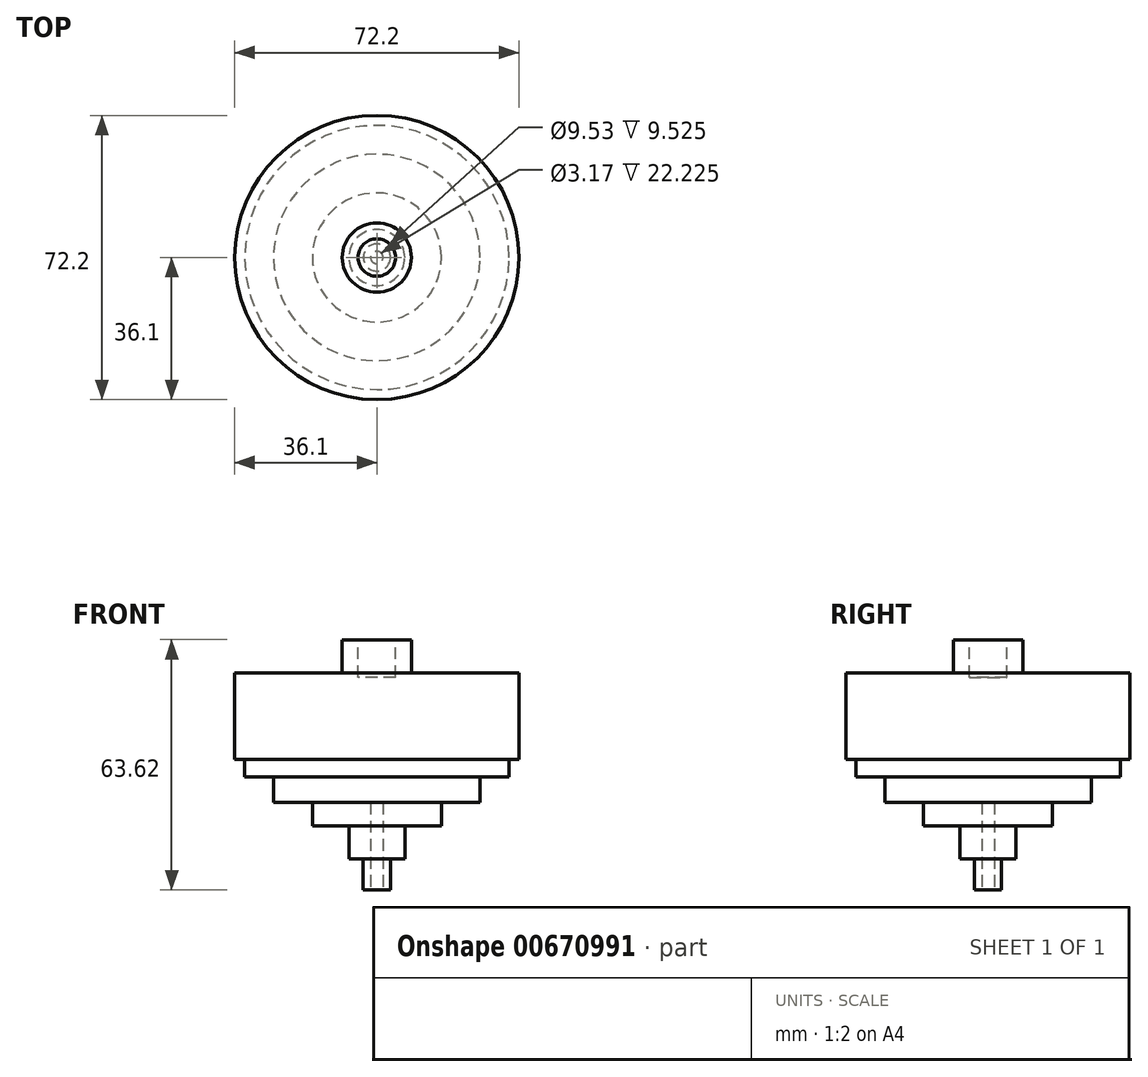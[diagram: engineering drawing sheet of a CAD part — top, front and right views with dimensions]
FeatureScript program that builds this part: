
annotation { "Feature Type Name" : "Feature", "Feature Type Description" : "" }
export const myFeature = defineFeature(function(context is Context, id is Id, definition is map)
    precondition{}
    {
        {
            var Q0;
            Q0=qCreatedBy(makeId("Front.planeOp"),FACE);
            var sketch = newSketch(context, id + "F0", { "sketchPlane" : qUnion([Q0])});
            skLineSegment(sketch, "E0", {"start": v(0, 26.1) * mm, "end": v(8.8, 26.1) * mm});
            skLineSegment(sketch, "E1", {"start": v(8.8, 26.1) * mm, "end": v(8.8, 17.66) * mm});
            skLineSegment(sketch, "E2", {"start": v(8.8, 17.66) * mm, "end": v(36.1, 17.66) * mm});
            skLineSegment(sketch, "E3", {"start": v(36.1, 17.66) * mm, "end": v(36.1, -4.3) * mm});
            skLineSegment(sketch, "E4", {"start": v(36.1, -4.3) * mm, "end": v(33.57, -4.3) * mm});
            skLineSegment(sketch, "E5", {"start": v(33.57, -4.3) * mm, "end": v(33.57, -8.8) * mm});
            skLineSegment(sketch, "E6", {"start": v(33.57, -8.8) * mm, "end": v(26.25, -8.8) * mm});
            skLineSegment(sketch, "E7", {"start": v(26.25, -8.8) * mm, "end": v(26.25, -15.27) * mm});
            skLineSegment(sketch, "E8", {"start": v(26.25, -15.27) * mm, "end": v(16.4, -15.27) * mm});
            skLineSegment(sketch, "E9", {"start": v(16.4, -15.27) * mm, "end": v(16.4, -21.19) * mm});
            skLineSegment(sketch, "E10", {"start": v(16.4, -21.19) * mm, "end": v(7.1, -21.19) * mm});
            skLineSegment(sketch, "E11", {"start": v(7.1, -21.19) * mm, "end": v(7.1, -29.63) * mm});
            skLineSegment(sketch, "E12", {"start": v(7.1, -29.63) * mm, "end": v(3.44, -29.63) * mm});
            skLineSegment(sketch, "E13", {"start": v(3.44, -29.63) * mm, "end": v(3.44, -37.51) * mm});
            skLineSegment(sketch, "E14", {"start": v(3.44, -37.51) * mm, "end": v(0, -37.51) * mm});
            skLineSegment(sketch, "E15", {"start": v(0, -37.51) * mm, "end": v(0, 26.1) * mm});
            skSolve(sketch);
        }
        {
            var Q0;
            Q0=makeQuery(id+"F0.imprint","IMPRINT",FACE,{"disambiguationData":[TD([[makeQuery(id+"F0.imprint","IMPRINT",EDGE,{"derivedFrom":sQuery(id+"F0.wireOp",EDGE,"E0")}),-1.0]])]});
            var Q1;
            Q1=sQuery(id+"F0.wireOp",EDGE,"E15");
            revolve(context, id + "F1", {"entities" : qUnion([Q0]), "axis" : qUnion([Q1]), "revolveType" : RevolveType.FULL});
        }
        {
            var Q0;
            Q0=makeQuery(id+"F1.opRevolve","SWEPT_FACE",FACE,{"disambiguationData":[OSD([sQuery(id+"F0.wireOp",EDGE,"E0")])]});
            var sketch = newSketch(context, id + "F2", { "sketchPlane" : qUnion([Q0])});
            skCircle(sketch, "E16", {"center": v(0, 0) * mm, "radius": 4.76 * mm});
            skSolve(sketch);
        }
        {
            var Q0;
            Q0 = qSketchRegion(id + "F2", true);
            extrude(context, id + "F3", {"entities" : qUnion([Q0]), "operationType" : NewBodyOperationType.REMOVE, "oppositeDirection" : true, "depth" : 9.52 * mm, "offsetDistance" : 25.4 * mm});
        }
        {
            var Q0;
            Q0=makeQuery(id+"F1.opRevolve","SWEPT_FACE",FACE,{"disambiguationData":[OSD([sQuery(id+"F0.wireOp",EDGE,"E14")])]});
            var sketch = newSketch(context, id + "F4", { "sketchPlane" : qUnion([Q0])});
            skCircle(sketch, "E17", {"center": v(0, 0) * mm, "radius": 1.59 * mm});
            skSolve(sketch);
        }
        {
            var Q0;
            Q0 = qSketchRegion(id + "F4", true);
            extrude(context, id + "F5", {"entities" : qUnion([Q0]), "operationType" : NewBodyOperationType.REMOVE, "oppositeDirection" : true, "depth" : 22.22 * mm, "offsetDistance" : 25.4 * mm});
        }
    });
